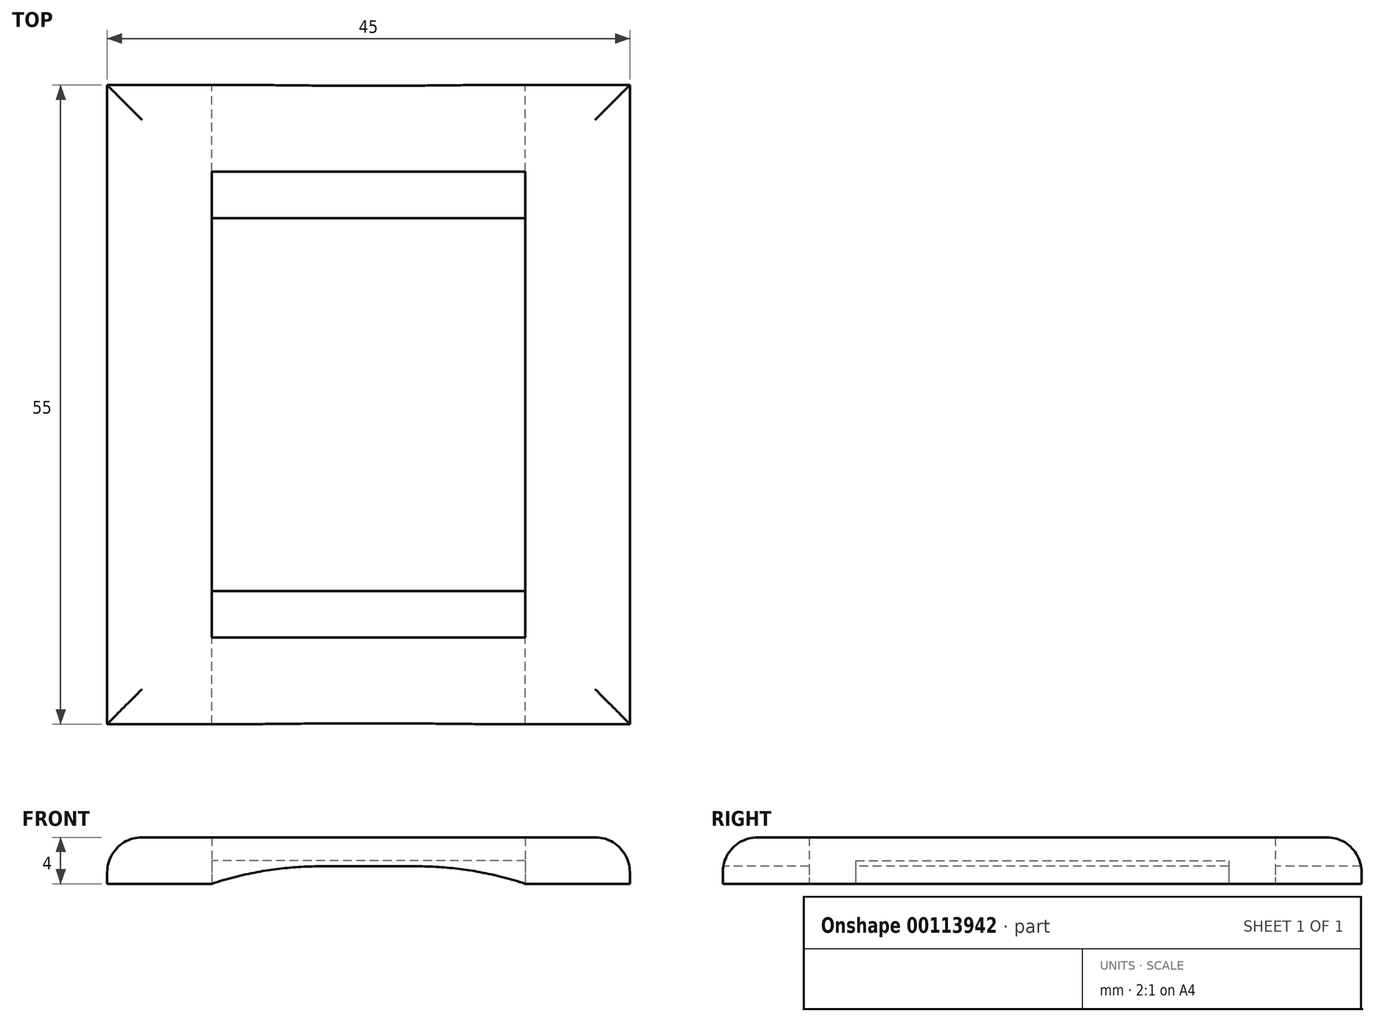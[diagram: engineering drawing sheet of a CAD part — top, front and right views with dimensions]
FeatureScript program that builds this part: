
annotation { "Feature Type Name" : "Feature", "Feature Type Description" : "" }
export const myFeature = defineFeature(function(context is Context, id is Id, definition is map)
    precondition{}
    {
        {
            var Q0;
            Q0=qCreatedBy(makeId("Top.planeOp"),FACE);
            var sketch = newSketch(context, id + "F0", { "sketchPlane" : qUnion([Q0])});
            skLineSegment(sketch, "E0.bottom", {"start": v(22.5, -27.5) * mm, "end": v(-22.5, -27.5) * mm});
            skLineSegment(sketch, "E0.top", {"start": v(22.5, 27.5) * mm, "end": v(-22.5, 27.5) * mm});
            skLineSegment(sketch, "E0.left", {"start": v(22.5, -27.5) * mm, "end": v(22.5, 27.5) * mm});
            skLineSegment(sketch, "E0.right", {"start": v(-22.5, -27.5) * mm, "end": v(-22.5, 27.5) * mm});
            skPoint(sketch, "E0.middle", {"position": v(0, 0) * mm});
            skLineSegment(sketch, "E1", {"start": v(-22.9, 0) * mm, "end": v(29.76, 0) * mm, "construction": true});
            skPoint(sketch, "E1.endSnap0", {"position": v(22.5, 0) * mm});
            skLineSegment(sketch, "E2", {"start": v(0, 27.5) * mm, "end": v(0, -27.5) * mm, "construction": true});
            skLineSegment(sketch, "E3.bottom", {"start": v(13.5, -20.06) * mm, "end": v(-13.5, -20.06) * mm});
            skLineSegment(sketch, "E3.top", {"start": v(13.5, -16.06) * mm, "end": v(-13.5, -16.06) * mm});
            skLineSegment(sketch, "E3.left", {"start": v(13.5, -20.06) * mm, "end": v(13.5, -16.06) * mm});
            skLineSegment(sketch, "E3.right", {"start": v(-13.5, -20.06) * mm, "end": v(-13.5, -16.06) * mm});
            skPoint(sketch, "E3.middle", {"position": v(0, -18.06) * mm});
            skPoint(sketch, "E4.MirrorP", {"position": v(0, 18.06) * mm});
            skLineSegment(sketch, "E5.MirrorCS", {"start": v(-13.5, 20.06) * mm, "end": v(-13.5, 16.06) * mm});
            skLineSegment(sketch, "E6.MirrorCS", {"start": v(13.5, 20.06) * mm, "end": v(13.5, 16.06) * mm});
            skLineSegment(sketch, "E7.MirrorCS", {"start": v(13.5, 20.06) * mm, "end": v(-13.5, 20.06) * mm});
            skLineSegment(sketch, "E8.MirrorCS", {"start": v(13.5, 16.06) * mm, "end": v(-13.5, 16.06) * mm});
            skSolve(sketch);
        }
        {
            var Q0;
            Q0=makeQuery(id+"F0.imprint","IMPRINT",FACE,{"disambiguationData":[TD([[makeQuery(id+"F0.imprint","IMPRINT",EDGE,{"derivedFrom":sQuery(id+"F0.wireOp",EDGE,"E0.bottom")}),-1.0]])]});
            extrude(context, id + "F1", {"entities" : qUnion([Q0]), "depth" : 4 * mm});
        }
        {
            var Q0;
            Q0=makeQuery(id+"F1.opExtrude","CAP_EDGE",EDGE,{"disambiguationData":[OSD([sQuery(id+"F0.wireOp",EDGE,"E0.left")])],"isStart":false});
            var Q1;
            Q1=makeQuery(id+"F1.opExtrude","CAP_EDGE",EDGE,{"disambiguationData":[OSD([sQuery(id+"F0.wireOp",EDGE,"E0.bottom")])],"isStart":false});
            var Q2;
            Q2=makeQuery(id+"F1.opExtrude","CAP_EDGE",EDGE,{"disambiguationData":[OSD([sQuery(id+"F0.wireOp",EDGE,"E0.right")])],"isStart":false});
            var Q3;
            Q3=makeQuery(id+"F1.opExtrude","CAP_EDGE",EDGE,{"disambiguationData":[OSD([sQuery(id+"F0.wireOp",EDGE,"E0.top")])],"isStart":false});
            fillet(context, id + "F2", {"entities" : qUnion([Q0, Q1, Q2, Q3]), "radius" : 3 * mm, "tangentPropagation" : true, "allowEdgeOverflow" : false});
        }
        {
            var Q0;
            Q0=makeQuery(id+"F1.opExtrude","CAP_FACE",FACE,{"disambiguationData":[OSD([sQuery(id+"F0.wireOp",EDGE,"E0.bottom"),sQuery(id+"F0.wireOp",EDGE,"E0.top"),sQuery(id+"F0.wireOp",EDGE,"E0.left"),sQuery(id+"F0.wireOp",EDGE,"E0.right"),sQuery(id+"F0.wireOp",EDGE,"E3.bottom"),sQuery(id+"F0.wireOp",EDGE,"E3.top"),sQuery(id+"F0.wireOp",EDGE,"E3.left"),sQuery(id+"F0.wireOp",EDGE,"E3.right"),sQuery(id+"F0.wireOp",EDGE,"E5.MirrorCS"),sQuery(id+"F0.wireOp",EDGE,"E6.MirrorCS"),sQuery(id+"F0.wireOp",EDGE,"E7.MirrorCS"),sQuery(id+"F0.wireOp",EDGE,"E8.MirrorCS")])],"isStart":false});
            var sketch = newSketch(context, id + "F3", { "sketchPlane" : qUnion([Q0])});
            skLineSegment(sketch, "E9", {"start": v(13.5, -16.06) * mm, "end": v(13.5, 16.06) * mm});
            skLineSegment(sketch, "E10", {"start": v(13.5, 16.06) * mm, "end": v(-13.5, 16.06) * mm});
            skLineSegment(sketch, "E11", {"start": v(-13.5, 16.06) * mm, "end": v(-13.5, -16.06) * mm});
            skLineSegment(sketch, "E12", {"start": v(-13.5, -16.06) * mm, "end": v(13.5, -16.06) * mm});
            skSolve(sketch);
        }
        {
            var Q0;
            Q0=makeQuery(id+"F3.imprint","IMPRINT",FACE,{"disambiguationData":[TD([[makeQuery(id+"F3.imprint","IMPRINT",EDGE,{"derivedFrom":sQuery(id+"F3.wireOp",EDGE,"E9")}),1.0]])]});
            extrude(context, id + "F4", {"entities" : qUnion([Q0]), "operationType" : NewBodyOperationType.REMOVE, "oppositeDirection" : true, "depth" : 2 * mm});
        }
        {
            var Q0;
            Q0=makeQuery(id+"F1.opExtrude","CAP_FACE",FACE,{"disambiguationData":[OSD([sQuery(id+"F0.wireOp",EDGE,"E0.bottom"),sQuery(id+"F0.wireOp",EDGE,"E0.top"),sQuery(id+"F0.wireOp",EDGE,"E0.left"),sQuery(id+"F0.wireOp",EDGE,"E0.right"),sQuery(id+"F0.wireOp",EDGE,"E3.bottom"),sQuery(id+"F0.wireOp",EDGE,"E3.top"),sQuery(id+"F0.wireOp",EDGE,"E3.left"),sQuery(id+"F0.wireOp",EDGE,"E3.right"),sQuery(id+"F0.wireOp",EDGE,"E5.MirrorCS"),sQuery(id+"F0.wireOp",EDGE,"E6.MirrorCS"),sQuery(id+"F0.wireOp",EDGE,"E7.MirrorCS"),sQuery(id+"F0.wireOp",EDGE,"E8.MirrorCS")])],"isStart":true});
            var sketch = newSketch(context, id + "F5", { "sketchPlane" : qUnion([Q0])});
            skLineSegment(sketch, "E13.bottom", {"start": v(13.5, -27.5) * mm, "end": v(-13.5, -27.5) * mm});
            skLineSegment(sketch, "E13.top", {"start": v(13.5, 27.5) * mm, "end": v(-13.5, 27.5) * mm});
            skLineSegment(sketch, "E13.left", {"start": v(13.5, -27.5) * mm, "end": v(13.5, 27.5) * mm});
            skLineSegment(sketch, "E13.right", {"start": v(-13.5, -27.5) * mm, "end": v(-13.5, 27.5) * mm});
            skPoint(sketch, "E13.middle", {"position": v(0, 0) * mm});
            skSolve(sketch);
        }
        {
            var Q0;
            Q0 = qSketchRegion(id + "F5", true);
            extrude(context, id + "F6", {"entities" : qUnion([Q0]), "operationType" : NewBodyOperationType.REMOVE, "oppositeDirection" : true, "depth" : 1.5 * mm});
        }
        {
            var Q0;
            {var subQ0=sQuery(id+"F5.wireOp",EDGE,"E13.right");Q0=makeQuery(id+"F6.boolean.opBoolean","COPY",EDGE,{"disambiguationData":[TD([makeQuery(id+"F1.opExtrude","SWEPT_FACE",FACE,{"disambiguationData":[OSD([sQuery(id+"F0.wireOp",EDGE,"E3.top")])]})])],"derivedFrom":makeQuery(id+"F6.opExtrude","CAP_EDGE",EDGE,{"disambiguationData":[OSD([subQ0])],"isStart":false})});}
            var Q1;
            {var subQ0=sQuery(id+"F5.wireOp",EDGE,"E13.right");Q1=makeQuery(id+"F6.boolean.opBoolean","COPY",EDGE,{"disambiguationData":[TD([makeQuery(id+"F1.opExtrude","SWEPT_FACE",FACE,{"disambiguationData":[OSD([sQuery(id+"F0.wireOp",EDGE,"E3.bottom")])]})])],"derivedFrom":makeQuery(id+"F6.opExtrude","CAP_EDGE",EDGE,{"disambiguationData":[OSD([subQ0])],"isStart":false})});}
            var Q2;
            {var subQ0=sQuery(id+"F5.wireOp",EDGE,"E13.right");Q2=makeQuery(id+"F6.boolean.opBoolean","COPY",EDGE,{"disambiguationData":[TD([makeQuery(id+"F1.opExtrude","SWEPT_FACE",FACE,{"disambiguationData":[OSD([sQuery(id+"F0.wireOp",EDGE,"E7.MirrorCS")])]})])],"derivedFrom":makeQuery(id+"F6.opExtrude","CAP_EDGE",EDGE,{"disambiguationData":[OSD([subQ0])],"isStart":false})});}
            var Q3;
            {var subQ0=sQuery(id+"F5.wireOp",EDGE,"E13.left");Q3=makeQuery(id+"F6.boolean.opBoolean","COPY",EDGE,{"disambiguationData":[TD([makeQuery(id+"F1.opExtrude","SWEPT_FACE",FACE,{"disambiguationData":[OSD([sQuery(id+"F0.wireOp",EDGE,"E3.top")])]})])],"derivedFrom":makeQuery(id+"F6.opExtrude","CAP_EDGE",EDGE,{"disambiguationData":[OSD([subQ0])],"isStart":false})});}
            var Q4;
            {var subQ0=sQuery(id+"F5.wireOp",EDGE,"E13.left");Q4=makeQuery(id+"F6.boolean.opBoolean","COPY",EDGE,{"disambiguationData":[TD([makeQuery(id+"F1.opExtrude","SWEPT_FACE",FACE,{"disambiguationData":[OSD([sQuery(id+"F0.wireOp",EDGE,"E3.bottom")])]})])],"derivedFrom":makeQuery(id+"F6.opExtrude","CAP_EDGE",EDGE,{"disambiguationData":[OSD([subQ0])],"isStart":false})});}
            var Q5;
            {var subQ0=sQuery(id+"F5.wireOp",EDGE,"E13.left");Q5=makeQuery(id+"F6.boolean.opBoolean","COPY",EDGE,{"disambiguationData":[TD([makeQuery(id+"F1.opExtrude","SWEPT_FACE",FACE,{"disambiguationData":[OSD([sQuery(id+"F0.wireOp",EDGE,"E7.MirrorCS")])]})])],"derivedFrom":makeQuery(id+"F6.opExtrude","CAP_EDGE",EDGE,{"disambiguationData":[OSD([subQ0])],"isStart":false})});}
            fillet(context, id + "F7", {"entities" : qUnion([Q0, Q1, Q2, Q3, Q4, Q5]), "radius" : 30 * mm, "tangentPropagation" : true, "allowEdgeOverflow" : false});
        }
    });
